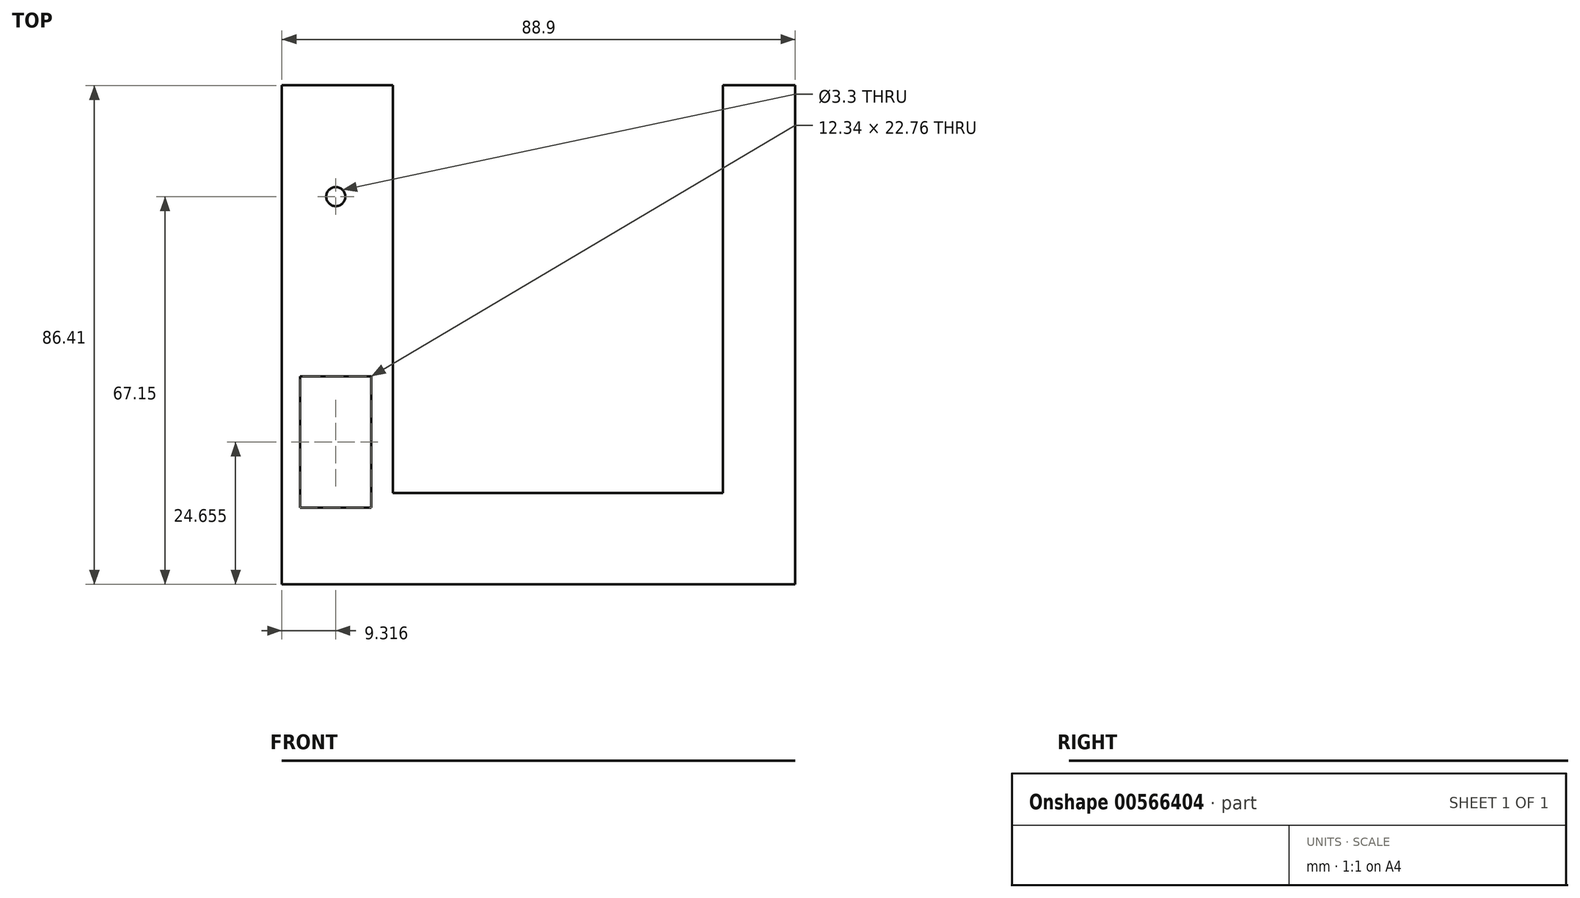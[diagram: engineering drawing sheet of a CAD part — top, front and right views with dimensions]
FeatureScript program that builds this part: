
annotation { "Feature Type Name" : "Feature", "Feature Type Description" : "" }
export const myFeature = defineFeature(function(context is Context, id is Id, definition is map)
    precondition{}
    {
        {
            var Q0;
            Q0=qCreatedBy(makeId("Top.planeOp"),FACE);
            var sketch = newSketch(context, id + "F0", { "sketchPlane" : qUnion([Q0])});
            skLineSegment(sketch, "E0.bottom", {"start": v(0, 0) * mm, "end": v(19.22, 0) * mm});
            skLineSegment(sketch, "E0.top", {"start": v(0, 86.41) * mm, "end": v(19.22, 86.41) * mm});
            skLineSegment(sketch, "E0.left", {"start": v(0, 0) * mm, "end": v(0, 86.41) * mm});
            skLineSegment(sketch, "E0.right", {"start": v(19.22, 15.84) * mm, "end": v(19.22, 86.41) * mm});
            skLineSegment(sketch, "E1.bottom", {"start": v(19.22, 0) * mm, "end": v(88.9, 0) * mm});
            skLineSegment(sketch, "E1.top", {"start": v(19.22, 15.84) * mm, "end": v(76.37, 15.84) * mm});
            skLineSegment(sketch, "E1.right", {"start": v(88.9, 0) * mm, "end": v(88.9, 15.84) * mm});
            skLineSegment(sketch, "E2.top", {"start": v(88.9, 86.41) * mm, "end": v(76.37, 86.41) * mm});
            skLineSegment(sketch, "E2.left", {"start": v(88.9, 15.84) * mm, "end": v(88.9, 86.41) * mm});
            skLineSegment(sketch, "E2.right", {"start": v(76.37, 15.84) * mm, "end": v(76.37, 86.41) * mm});
            skLineSegment(sketch, "E3.bottom", {"start": v(3.14, 13.28) * mm, "end": v(15.49, 13.28) * mm});
            skLineSegment(sketch, "E3.top", {"start": v(3.14, 36.03) * mm, "end": v(15.49, 36.03) * mm});
            skLineSegment(sketch, "E3.left", {"start": v(3.14, 13.28) * mm, "end": v(3.14, 36.03) * mm});
            skLineSegment(sketch, "E3.right", {"start": v(15.49, 13.28) * mm, "end": v(15.49, 36.03) * mm});
            skCircle(sketch, "E4", {"center": v(9.32, 67.15) * mm, "radius": 1.65 * mm});
            skPoint(sketch, "E4.centerSnap0", {"position": v(9.32, 36.03) * mm});
            skCircle(sketch, "E5", {"center": v(9.32, 29.05) * mm, "radius": 2.82 * mm, "construction": true});
            skSolve(sketch);
        }
        {
            var Q0;
            Q0=makeQuery(id+"F0.imprint","IMPRINT",FACE,{"disambiguationData":[TD([[makeQuery(id+"F0.imprint","IMPRINT",EDGE,{"derivedFrom":sQuery(id+"F0.wireOp",EDGE,"E0.bottom")}),1.0]])]});
            extrude(context, id + "F1", {"entities" : qUnion([Q0]), "depth" : 1 / 203.2 * mm, "offsetDistance" : 25.4 * mm});
        }
    });
